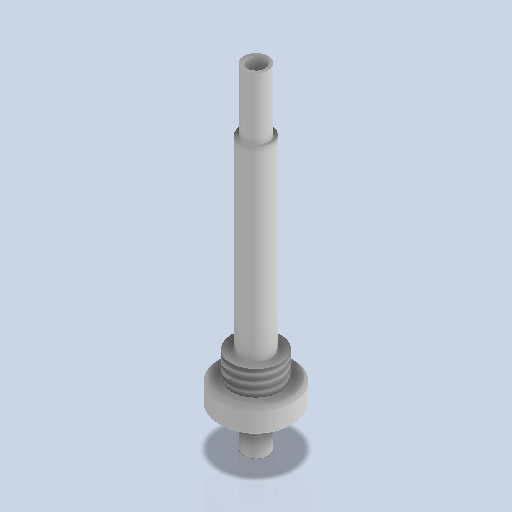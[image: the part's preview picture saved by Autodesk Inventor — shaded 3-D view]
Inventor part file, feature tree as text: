
AUTODESK INVENTOR PART (.ipt)
format: ipt  version: 2024.2 (Build 282272000, 272)  size: 296,448 bytes
history: native  units: mm
features: chamfer x2, sketch x2, revolve x1, thread x1, hole x1
ambient origin geometry x8: Origin, YZ Plane, XZ Plane, XY Plane, X Axis, Y Axis, Z Axis, Center Point
bodies: Volumenkörper1 (feature_tree)
feature tree (7):
  revolve  "Umdrehung1"
  thread  "Gewinde1"  [1 undecoded]
  chamfer  "Fasen1"  Distance=4.0mm
  chamfer  "Fasen2"  Distance=4.0mm
  hole  "Bohrung1"  [1 undecoded]
  sketch  "Skizze1"  dims[d1=36.0mm]
  sketch  "Skizze2"  dims[d2=4.0mm d3=4.0mm d4=4.0mm d5=12.0mm d6=5.0mm d7=8.0mm d8=8.0mm d11=10.0mm d12=6.0mm d13=90.0deg d14=18.0mm d15=0.0mm d16=0.5mm d17=2.0mm d18=45.0deg d19=0.5mm d20=2.0mm d21=45.0deg d23=3.0mm d24=6.0mm d25=4.0mm d26=2.0mm d27=90.0deg d28=8.0mm d29=20.594885mm]
note: 2 required parameter values undecoded (feature->parameter linkage not recoverable at this tier; creation-order binding heuristic only, values carry confidence <= 0.55)
